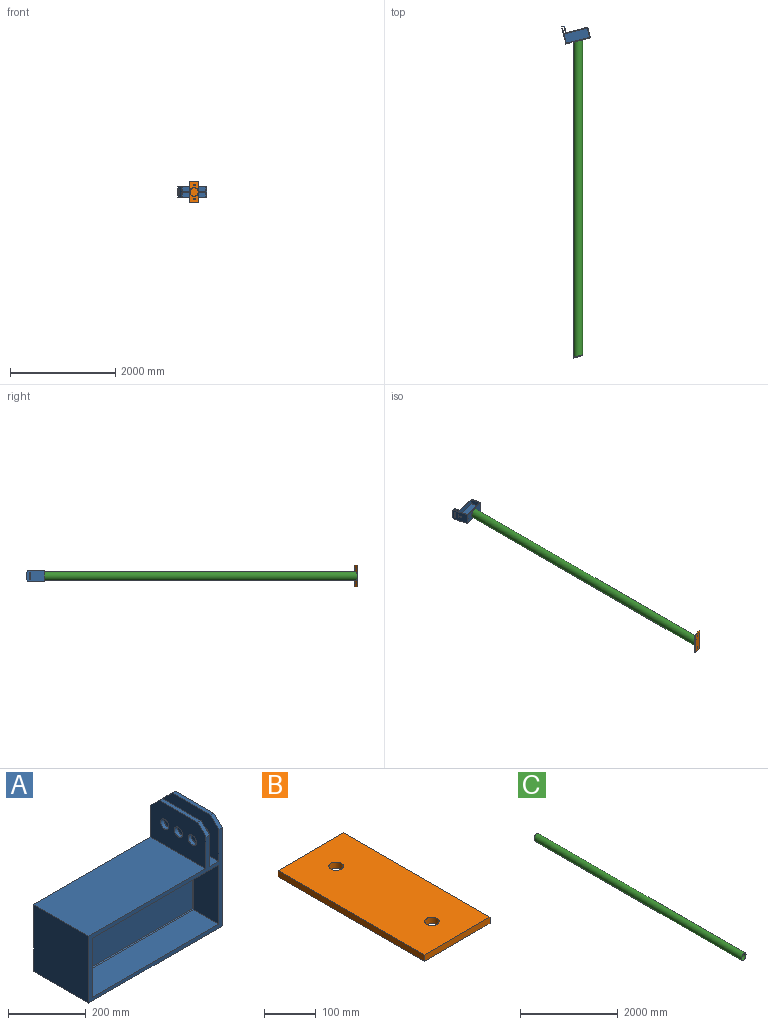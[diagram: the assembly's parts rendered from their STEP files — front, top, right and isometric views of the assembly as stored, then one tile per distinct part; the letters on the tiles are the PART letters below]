
ASSEMBLY  parts=3 mates=2
PART A: 40 faces, bbox 485x200x340 mm
  f0: plane 140x12mm, normal (0,0,1), area 1680mm2, adj f3,f4,f36,f37
  f1: plane 140x12mm, normal (0,0,1), area 1680mm2, adj f2,f5,f38,f39
  f2: plane 200x130mm, normal (-1,0,0), area 22979.4mm2, adj f1,f13,f18,f19,f30,f31,f32,f38
  f3: plane 200x130mm, normal (1,0,0), area 22979.4mm2, adj f0,f13,f18,f19,f33,f34,f35,f36
  f4: plane 200x130mm, normal (-1,0,0), area 22979.4mm2, adj f0,f14,f18,f19,f33,f34,f35,f36
  f5: plane 340x200mm, normal (1,0,0), area 64979.4mm2, adj f1,f16,f18,f19,f30,f31,f32,f38
  f6: plane 461x91mm, normal (0,0,-1), area 41951mm2, adj f7,f9,f19,f23
  f7: plane 186x91mm, normal (-1,0,0), area 16926mm2, adj f6,f8,f19,f22
  f8: plane 461x91mm, normal (0,0,1), area 41951mm2, adj f7,f9,f19,f24
  f9: plane 186x91mm, normal (1,0,0), area 16926mm2, adj f6,f8,f19,f25
  f10: plane 461x91mm, normal (0,0,-1), area 41951mm2, adj f11,f17,f18,f26
  f11: plane 186x91mm, normal (-1,0,0), area 16926mm2, adj f10,f12,f18,f27
  f12: plane 461x91mm, normal (0,0,1), area 41951mm2, adj f11,f17,f18,f29
  f13: plane 200x35mm, normal (0,0,1), area 7000mm2, adj f2,f3,f18,f19
  f14: plane 426x200mm, normal (0,0,1), area 85200mm2, adj f4,f15,f18,f19
  f15: plane 210x200mm, normal (-1,0,0), area 42000mm2, adj f14,f16,f18,f19
  f16: plane 485x200mm, normal (0,0,-1), area 97000mm2, adj f5,f15,f18,f19
  f17: plane 186x91mm, normal (1,0,0), area 16926mm2, adj f10,f12,f18,f28
  f18: plane 485x310mm, normal (0,-1,0), area 18504mm2, adj f2,f3,f4,f5,f10,f11,f12,f13
  f19: plane 485x310mm, normal (0,1,0), area 18504mm2, adj f2,f3,f4,f5,f6,f7,f8,f9
  f20: plane 455x180mm, normal (0,-1,0), area 81900mm2, adj f26,f27,f28,f29
  f21: plane 455x180mm, normal (0,1,0), area 81900mm2, adj f22,f23,f24,f25
  f22: plane 186x3mm, normal (-0.71,0.71,0), area 776.4mm2, adj f7,f21,f23,f24
  f23: plane 461x3mm, normal (0,0.71,-0.71), area 1943.1mm2, adj f6,f21,f22,f25
  f24: plane 461x3mm, normal (0,0.71,0.71), area 1943.1mm2, adj f8,f21,f22,f25
  f25: plane 186x3mm, normal (0.71,0.71,0), area 776.4mm2, adj f9,f21,f23,f24
  f26: plane 461x3mm, normal (0,-0.71,-0.71), area 1943.1mm2, adj f10,f20,f27,f28
  f27: plane 186x3mm, normal (-0.71,-0.71,0), area 776.4mm2, adj f11,f20,f26,f29
  f28: plane 186x3mm, normal (0.71,-0.71,0), area 776.4mm2, adj f17,f20,f26,f29
  f29: plane 461x3mm, normal (0,-0.71,0.71), area 1943.1mm2, adj f12,f20,f27,f28
  f30: cylinder r=15mm len=30mm, axis (1,0,0), area 1131mm2, adj f2,f5
  f31: cylinder r=15mm len=30mm, axis (1,0,0), area 1131mm2, adj f2,f5
  f32: cylinder r=15mm len=30mm, axis (1,0,0), area 1131mm2, adj f2,f5
  f33: cylinder r=15mm len=30mm, axis (1,0,0), area 1131mm2, adj f3,f4
  f34: cylinder r=15mm len=30mm, axis (1,0,0), area 1131mm2, adj f3,f4
  f35: cylinder r=15mm len=30mm, axis (1,0,0), area 1131mm2, adj f3,f4
  f36: plane 30x30mm, normal (0,-0.71,0.71), area 509.1mm2, adj f0,f3,f4,f18
  f37: plane 30x30mm, normal (0,0.71,0.71), area 509.1mm2, adj f0,f3,f4,f19
  f38: plane 30x30mm, normal (0,-0.71,0.71), area 509.1mm2, adj f1,f2,f5,f18
  f39: plane 30x30mm, normal (0,0.71,0.71), area 509.1mm2, adj f1,f2,f5,f19
PART B: 8 faces, bbox 180x400x15 mm
  f0: plane 400x15mm, normal (1,0,0), area 6000mm2, adj f1,f4,f6,f7
  f1: plane 180x15mm, normal (0,1,0), area 2700mm2, adj f0,f2,f6,f7
  f2: plane 400x15mm, normal (-1,0,0), area 6000mm2, adj f1,f4,f6,f7
  f3: cylinder r=14mm len=28mm, axis (0,0,-1), area 1319.5mm2, adj f6,f7
  f4: plane 180x15mm, normal (0,-1,0), area 2700mm2, adj f0,f2,f6,f7
  f5: cylinder r=14mm len=28mm, axis (0,0,-1), area 1319.5mm2, adj f6,f7
  f6: plane 400x180mm, normal (0,0,1), area 70768.5mm2, adj f0,f1,f2,f3,f4,f5
  f7: plane 400x180mm, normal (0,0,-1), area 70768.5mm2, adj f0,f1,f2,f3,f4,f5
PART C: 4 faces, bbox 168.3x6038.2x168.3 mm
  f0: cylinder r=79.65mm len=6035.98mm, axis (0,1,0), area 3000722.9mm2, adj f2,f3
  f1: cylinder r=84.15mm len=6038.24mm, axis (0,1,0), area 3170255.3mm2, adj f2,f3
  f2: plane 168.3x168.3mm, normal (-0.24,0.97,0), area 2386.6mm2, adj f0,f1
  f3: plane 168.3x168.3mm, normal (0.24,-0.97,0), area 2386.6mm2, adj f0,f1
PLACE A rot(axis=(0.09,-0.7,-0.7),170.1deg) t=(-25.4,3099.87,0)mm
PLACE B rot(axis=(-0.99,-0.12,0.12),90.9deg) t=(3.63,-3012.54,0)mm
PLACE C at identity
MATE fastened B.f6 <-> C.f3  axis (-0.24,0.97,0) through (0,-2997.99,0)mm
MATE fastened A.f16 <-> C.f2  axis (0.24,-0.97,0) through (0,2997.99,0)mm
